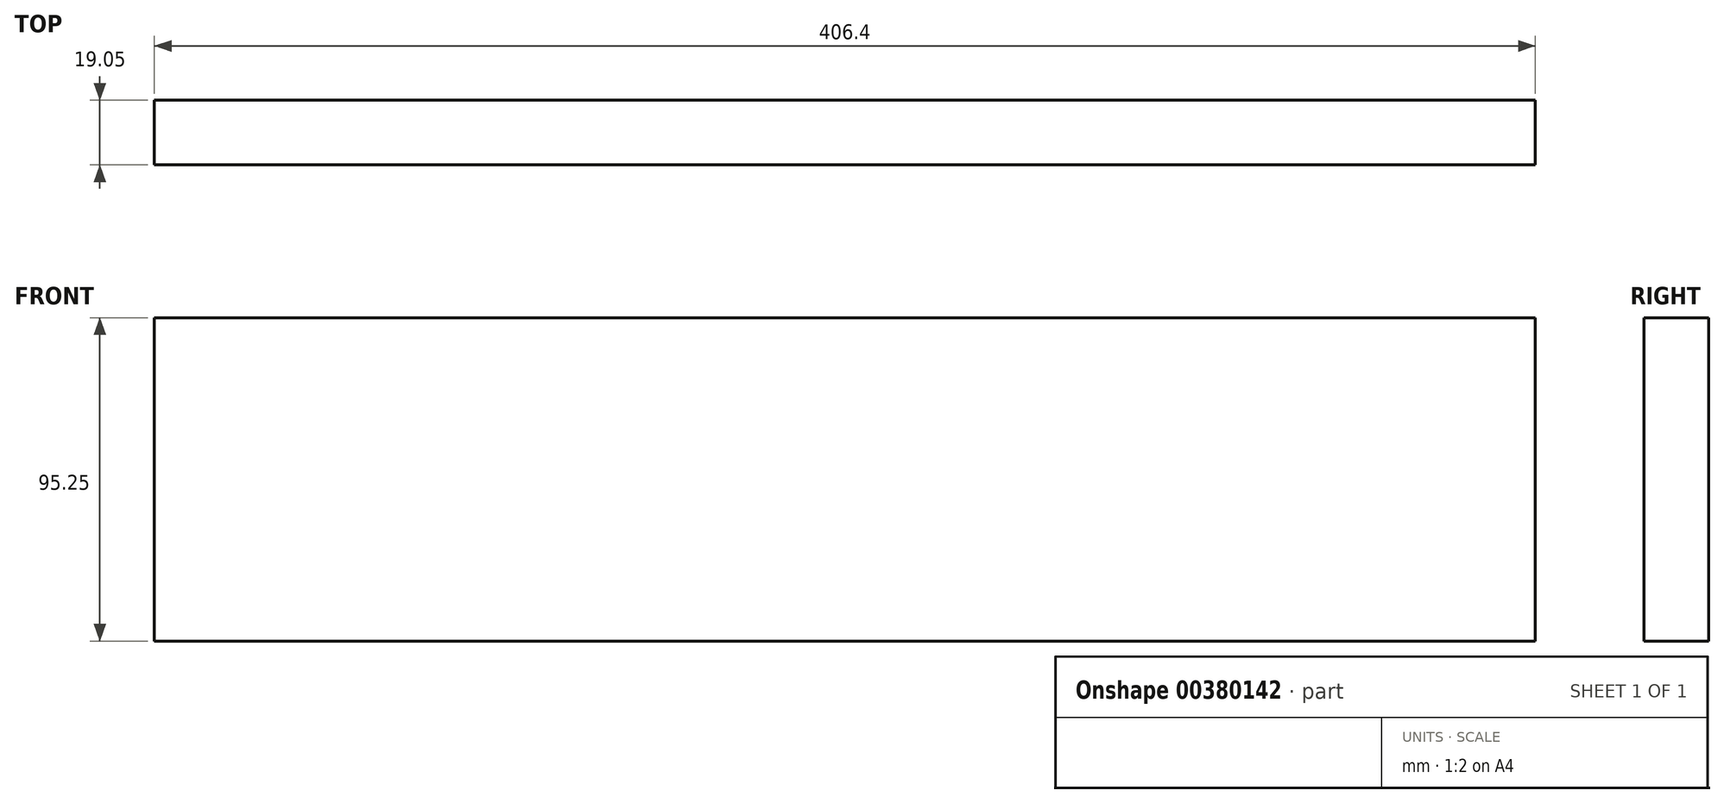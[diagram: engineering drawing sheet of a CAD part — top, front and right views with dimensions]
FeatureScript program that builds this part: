
annotation { "Feature Type Name" : "Feature", "Feature Type Description" : "" }
export const myFeature = defineFeature(function(context is Context, id is Id, definition is map)
    precondition{}
    {
        {
            var Q0;
            Q0=qCreatedBy(makeId("Front.planeOp"),FACE);
            var sketch = newSketch(context, id + "F0", { "sketchPlane" : qUnion([Q0])});
            skLineSegment(sketch, "E0.bottom", {"start": v(-203.2, 0) * mm, "end": v(203.2, 0) * mm});
            skLineSegment(sketch, "E0.top", {"start": v(-203.2, -95.25) * mm, "end": v(203.2, -95.25) * mm});
            skLineSegment(sketch, "E0.left", {"start": v(-203.2, 0) * mm, "end": v(-203.2, -95.25) * mm});
            skLineSegment(sketch, "E0.right", {"start": v(203.2, 0) * mm, "end": v(203.2, -95.25) * mm});
            skSolve(sketch);
        }
        {
            var Q0;
            Q0 = qSketchRegion(id + "F0", true);
            extrude(context, id + "F1", {"entities" : qUnion([Q0]), "depth" : 19.05 * mm});
        }
    });
